annotation { "Feature Type Name" : "Feature", "Feature Type Description" : "" }
export const myFeature = defineFeature(function(context is Context, id is Id, definition is map)
    precondition{}
    {
        {
            var Q0;
            Q0=qCreatedBy(makeId("Top.planeOp"),FACE);
            var sketch = newSketch(context, id + "F0", { "sketchPlane" : qUnion([Q0])});
            skLineSegment(sketch, "E0.bottom", {"start": v(57.81, -99.19) * mm, "end": v(-57.81, -99.19) * mm});
            skLineSegment(sketch, "E0.top", {"start": v(57.81, 99.19) * mm, "end": v(-57.81, 99.19) * mm});
            skLineSegment(sketch, "E0.left", {"start": v(57.81, -99.19) * mm, "end": v(57.81, 99.19) * mm});
            skLineSegment(sketch, "E0.right", {"start": v(-57.81, -99.19) * mm, "end": v(-57.81, 99.19) * mm});
            skPoint(sketch, "E0.middle", {"position": v(0, 0) * mm});
            skSolve(sketch);
        }
        {
            var Q0;
            Q0 = qSketchRegion(id + "F0", true);
            extrude(context, id + "F1", {"entities" : qUnion([Q0]), "offsetDistance" : 25.4 * mm, "depth" : 43.33 * mm});
        }
        {
            var Q0;
            Q0=makeQuery(id+"F1.opExtrude","CAP_FACE",FACE,{"disambiguationData":[OSD([sQuery(id+"F0.wireOp",EDGE,"E0.bottom"),sQuery(id+"F0.wireOp",EDGE,"E0.top"),sQuery(id+"F0.wireOp",EDGE,"E0.left"),sQuery(id+"F0.wireOp",EDGE,"E0.right")])],"isStart":false});
            var sketch = newSketch(context, id + "F2", { "sketchPlane" : qUnion([Q0])});
            skLineSegment(sketch, "E1.bottom", {"start": v(50.67, -86.17) * mm, "end": v(-50.67, -86.17) * mm});
            skLineSegment(sketch, "E1.top", {"start": v(50.67, -10.6) * mm, "end": v(-50.67, -10.6) * mm});
            skLineSegment(sketch, "E1.left", {"start": v(50.67, -86.17) * mm, "end": v(50.67, -10.6) * mm});
            skLineSegment(sketch, "E1.right", {"start": v(-50.67, -86.17) * mm, "end": v(-50.67, -10.6) * mm});
            skPoint(sketch, "E1.middle", {"position": v(0, -48.39) * mm});
            skLineSegment(sketch, "E2", {"start": v(0, -48.39) * mm, "end": v(0, -99.19) * mm, "construction": true});
            skSolve(sketch);
        }
        {
            var Q0;
            Q0 = qSketchRegion(id + "F2", true);
            extrude(context, id + "F3", {"entities" : qUnion([Q0]), "operationType" : NewBodyOperationType.REMOVE, "oppositeDirection" : true, "offsetDistance" : 25.4 * mm, "depth" : 8 * mm});
        }
        {
            var Q0;
            Q0=makeQuery(id+"F1.opExtrude","CAP_FACE",FACE,{"disambiguationData":[OSD([sQuery(id+"F0.wireOp",EDGE,"E0.bottom"),sQuery(id+"F0.wireOp",EDGE,"E0.top"),sQuery(id+"F0.wireOp",EDGE,"E0.left"),sQuery(id+"F0.wireOp",EDGE,"E0.right")])],"isStart":false});
            var sketch = newSketch(context, id + "F4", { "sketchPlane" : qUnion([Q0])});
            skLineSegment(sketch, "E3.bottom", {"start": v(51.46, -92.84) * mm, "end": v(-51.46, -92.84) * mm});
            skLineSegment(sketch, "E3.top", {"start": v(51.46, 92.84) * mm, "end": v(-51.46, 92.84) * mm});
            skLineSegment(sketch, "E3.left", {"start": v(51.46, -92.84) * mm, "end": v(51.46, 92.84) * mm});
            skLineSegment(sketch, "E3.right", {"start": v(-51.46, -92.84) * mm, "end": v(-51.46, 92.84) * mm});
            skPoint(sketch, "E3.middle", {"position": v(0, 0) * mm});
            skLineSegment(sketch, "E4", {"start": v(0, 92.84) * mm, "end": v(0, 99.19) * mm, "construction": true});
            skLineSegment(sketch, "E5", {"start": v(-51.46, 0) * mm, "end": v(-57.81, 0) * mm, "construction": true});
            skSolve(sketch);
        }
        {
            var Q0;
            Q0 = qSketchRegion(id + "F4", true);
            extrude(context, id + "F5", {"entities" : qUnion([Q0]), "operationType" : NewBodyOperationType.REMOVE, "oppositeDirection" : true, "offsetDistance" : 25.4 * mm, "depth" : 5.46 * mm});
        }
        {
            var Q0;
            Q0=makeQuery(id+"F3.boolean.opBoolean","COPY",EDGE,{"derivedFrom":makeQuery(id+"F3.opExtrude","SWEPT_EDGE",EDGE,{"disambiguationData":[OSD([sQuery(id+"F2.wireOp",EDGE,"E1.top"),sQuery(id+"F2.wireOp",EDGE,"E1.right")])]})});
            var Q1;
            Q1=makeQuery(id+"F3.boolean.opBoolean","COPY",EDGE,{"derivedFrom":makeQuery(id+"F3.opExtrude","SWEPT_EDGE",EDGE,{"disambiguationData":[OSD([sQuery(id+"F2.wireOp",EDGE,"E1.top"),sQuery(id+"F2.wireOp",EDGE,"E1.left")])]})});
            var Q2;
            Q2=makeQuery(id+"F3.boolean.opBoolean","COPY",EDGE,{"derivedFrom":makeQuery(id+"F3.opExtrude","SWEPT_EDGE",EDGE,{"disambiguationData":[OSD([sQuery(id+"F2.wireOp",EDGE,"E1.bottom"),sQuery(id+"F2.wireOp",EDGE,"E1.left")])]})});
            var Q3;
            Q3=makeQuery(id+"F3.boolean.opBoolean","COPY",EDGE,{"derivedFrom":makeQuery(id+"F3.opExtrude","SWEPT_EDGE",EDGE,{"disambiguationData":[OSD([sQuery(id+"F2.wireOp",EDGE,"E1.bottom"),sQuery(id+"F2.wireOp",EDGE,"E1.right")])]})});
            fillet(context, id + "F6", {"entities" : qUnion([Q0, Q1, Q2, Q3]), "radius" : 12.7 * mm, "tangentPropagation" : true, "allowEdgeOverflow" : false});
        }
        {
            var Q0;
            Q0=makeQuery(id+"F5.boolean.opBoolean","COPY",EDGE,{"derivedFrom":makeQuery(id+"F5.opExtrude","SWEPT_EDGE",EDGE,{"disambiguationData":[OSD([sQuery(id+"F4.wireOp",EDGE,"E3.top"),sQuery(id+"F4.wireOp",EDGE,"E3.right")])]})});
            var Q1;
            Q1=makeQuery(id+"F5.boolean.opBoolean","COPY",EDGE,{"derivedFrom":makeQuery(id+"F5.opExtrude","SWEPT_EDGE",EDGE,{"disambiguationData":[OSD([sQuery(id+"F4.wireOp",EDGE,"E3.top"),sQuery(id+"F4.wireOp",EDGE,"E3.left")])]})});
            var Q2;
            Q2=makeQuery(id+"F5.boolean.opBoolean","COPY",EDGE,{"derivedFrom":makeQuery(id+"F5.opExtrude","SWEPT_EDGE",EDGE,{"disambiguationData":[OSD([sQuery(id+"F4.wireOp",EDGE,"E3.bottom"),sQuery(id+"F4.wireOp",EDGE,"E3.right")])]})});
            var Q3;
            Q3=makeQuery(id+"F5.boolean.opBoolean","COPY",EDGE,{"derivedFrom":makeQuery(id+"F5.opExtrude","SWEPT_EDGE",EDGE,{"disambiguationData":[OSD([sQuery(id+"F4.wireOp",EDGE,"E3.bottom"),sQuery(id+"F4.wireOp",EDGE,"E3.left")])]})});
            fillet(context, id + "F7", {"entities" : qUnion([Q0, Q1, Q2, Q3]), "radius" : 12.7 * mm, "tangentPropagation" : true, "allowEdgeOverflow" : false});
        }
        {
            var Q0;
            Q0=makeQuery(id+"F5.boolean.opBoolean","COPY",FACE,{"derivedFrom":makeQuery(id+"F5.opExtrude","CAP_FACE",FACE,{"disambiguationData":[OSD([sQuery(id+"F4.wireOp",EDGE,"E3.bottom"),sQuery(id+"F4.wireOp",EDGE,"E3.top"),sQuery(id+"F4.wireOp",EDGE,"E3.left"),sQuery(id+"F4.wireOp",EDGE,"E3.right")])],"isStart":false})});
            var sketch = newSketch(context, id + "F8", { "sketchPlane" : qUnion([Q0])});
            skLineSegment(sketch, "E6.0", {"start": v(-51.46, -80.14) * mm, "end": v(-51.46, 80.14) * mm});
            skLineSegment(sketch, "E6.1", {"start": v(38.76, 92.84) * mm, "end": v(-38.76, 92.84) * mm});
            skLineSegment(sketch, "E6.2", {"start": v(51.46, -80.14) * mm, "end": v(51.46, 80.14) * mm});
            skLineSegment(sketch, "E6.3", {"start": v(38.76, -92.84) * mm, "end": v(-38.76, -92.84) * mm});
            skArc(sketch, "E6.4", {"start": v(51.46, -80.14) * mm, "mid": v(47.74, -89.12) * mm, "end": v(38.76, -92.84) * mm});
            skArc(sketch, "E6.5", {"start": v(-38.76, -92.84) * mm, "mid": v(-47.74, -89.12) * mm, "end": v(-51.46, -80.14) * mm});
            skArc(sketch, "E6.6", {"start": v(-51.46, 80.14) * mm, "mid": v(-47.74, 89.12) * mm, "end": v(-38.76, 92.84) * mm});
            skArc(sketch, "E6.7", {"start": v(38.76, 92.84) * mm, "mid": v(47.74, 89.12) * mm, "end": v(51.46, 80.14) * mm});
            skSolve(sketch);
        }
        {
            var Q0;
            Q0 = qSketchRegion(id + "F8", true);
            extrude(context, id + "F9", {"entities" : qUnion([Q0]), "offsetDistance" : 25.4 * mm, "depth" : 6.35 * mm - 0.89 * mm});
        }
        {
            var Q0;
            Q0=makeQuery(id+"F1.opExtrude","CAP_EDGE",EDGE,{"disambiguationData":[OSD([sQuery(id+"F0.wireOp",EDGE,"E0.left")])],"isStart":false});
            var Q1;
            Q1=makeQuery(id+"F1.opExtrude","CAP_EDGE",EDGE,{"disambiguationData":[OSD([sQuery(id+"F0.wireOp",EDGE,"E0.top")])],"isStart":false});
            var Q2;
            Q2=makeQuery(id+"F1.opExtrude","CAP_EDGE",EDGE,{"disambiguationData":[OSD([sQuery(id+"F0.wireOp",EDGE,"E0.right")])],"isStart":false});
            var Q3;
            Q3=makeQuery(id+"F1.opExtrude","CAP_EDGE",EDGE,{"disambiguationData":[OSD([sQuery(id+"F0.wireOp",EDGE,"E0.bottom")])],"isStart":false});
            chamfer(context, id + "F10", {"entities" : qUnion([Q0, Q1, Q2, Q3]), "width" : 3.17 * mm, "tangentPropagation" : true});
        }
        {
            var Q0;
            Q0=makeQuery(id+"F5.boolean.opBoolean","COPY",FACE,{"derivedFrom":makeQuery(id+"F5.opExtrude","CAP_FACE",FACE,{"disambiguationData":[OSD([sQuery(id+"F4.wireOp",EDGE,"E3.bottom"),sQuery(id+"F4.wireOp",EDGE,"E3.top"),sQuery(id+"F4.wireOp",EDGE,"E3.left"),sQuery(id+"F4.wireOp",EDGE,"E3.right")])],"isStart":false})});
            var sketch = newSketch(context, id + "F11", { "sketchPlane" : qUnion([Q0])});
            skText(sketch, "E7", { "text": "Drew", "fontName": "Arimo-Bold.ttf"});
            skText(sketch, "E8", { "text": "Matthews", "fontName": "Arimo-Bold.ttf"});
            skLineSegment(sketch, "E9", {"start": v(0, -10.6) * mm, "end": v(0, 92.84) * mm, "construction": true});
            skLineSegment(sketch, "E10", {"start": v(27.32, 41.12) * mm, "end": v(24.14, 41.12) * mm, "construction": true});
            skLineSegment(sketch, "E11", {"start": v(9.54, 41.12) * mm, "end": v(0, 41.12) * mm, "construction": true});
            skText(sketch, "E12", { "text": "MASTER AUTOMOBILE", "fontName": "Arimo-Regular.ttf"});
            skLineSegment(sketch, "E13", {"start": v(-9.22, 41.12) * mm, "end": v(0, 41.12) * mm, "construction": true});
            skText(sketch, "E14", { "text": "TECHNICIAN", "fontName": "Arimo-Regular.ttf"});
            skLineSegment(sketch, "E15", {"start": v(-18.11, 41.12) * mm, "end": v(-14.94, 41.12) * mm, "construction": true});
            skText(sketch, "E16", { "text": "December 31, 2003", "fontName": "Arimo-Regular.ttf"});
            skLineSegment(sketch, "E17", {"start": v(-23.83, 41.12) * mm, "end": v(-36.53, 41.12) * mm, "construction": true});
            skLineSegment(sketch, "E18", {"start": v(41.92, 41.12) * mm, "end": v(51.46, 41.12) * mm, "construction": true});
            skLineSegment(sketch, "E19", {"start": v(-42.24, 41.12) * mm, "end": v(-51.46, 41.12) * mm, "construction": true});
            const initialGuessF11  = {"E7": [0.02732, 0.06664, 0, -1, 0.0146], "E8": [0.00954, 0.08761, 0, -1, 0.0146], "E12": [-0.01494, 0.08488, 0, -1, 0.00571], "E14": [-0.02383, 0.06532, 0, -1, 0.00572], "E16": [-0.04224, 0.07607, 0, -1, 0.00571]};
            skSetInitialGuess(sketch, initialGuessF11);
            skSolve(sketch);
        }
        {
            var Q0;
            Q0 = qSketchRegion(id + "F11", true);
            extrude(context, id + "F12", {"entities" : qUnion([Q0]), "operationType" : NewBodyOperationType.REMOVE, "oppositeDirection" : true, "depth" : 0.64 * mm, "offsetDistance" : 25.4 * mm});
        }
    });